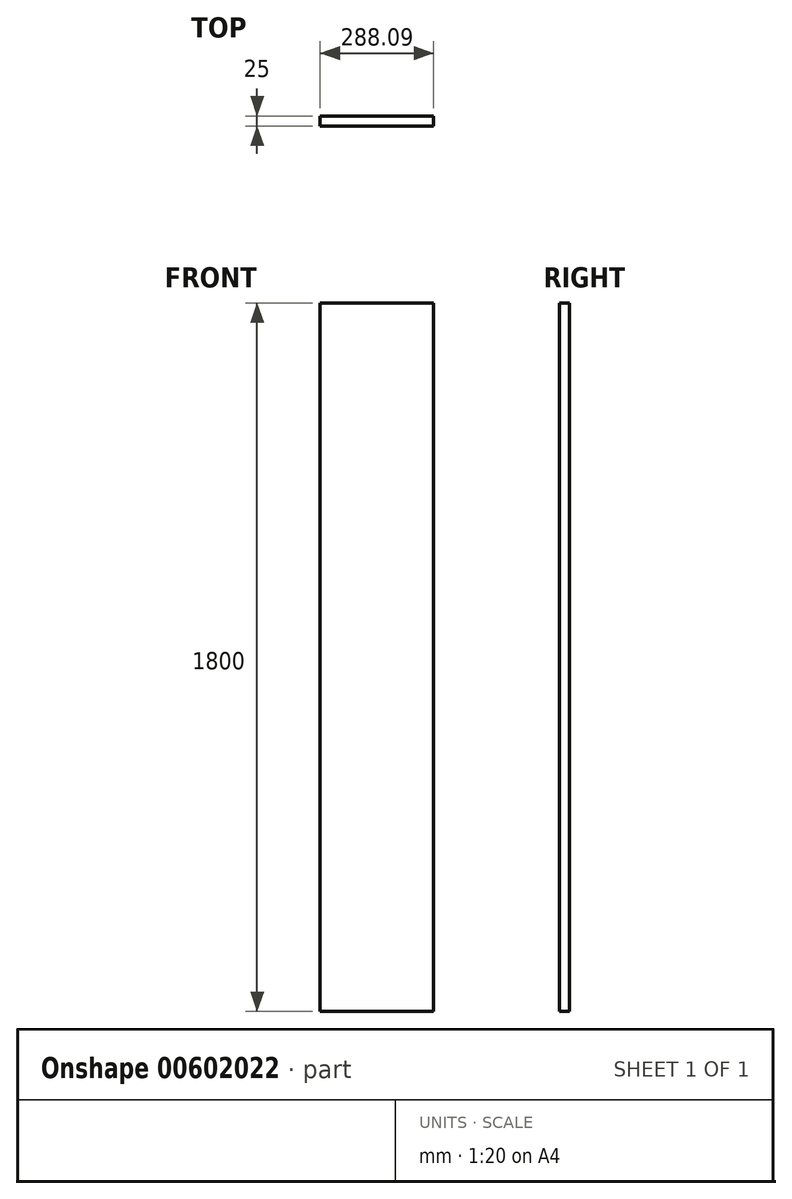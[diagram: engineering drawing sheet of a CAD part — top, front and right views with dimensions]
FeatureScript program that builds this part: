
annotation { "Feature Type Name" : "Feature", "Feature Type Description" : "" }
export const myFeature = defineFeature(function(context is Context, id is Id, definition is map)
    precondition{}
    {
        {
            var Q0;
            Q0=qCreatedBy(makeId("Front.planeOp"),FACE);
            var sketch = newSketch(context, id + "F0", { "sketchPlane" : qUnion([Q0])});
            skLineSegment(sketch, "E0.bottom", {"start": v(0, 0) * mm, "end": v(288.09, 0) * mm});
            skLineSegment(sketch, "E0.top", {"start": v(0, 1800) * mm, "end": v(288.09, 1800) * mm});
            skLineSegment(sketch, "E0.left", {"start": v(0, 0) * mm, "end": v(0, 1800) * mm});
            skLineSegment(sketch, "E0.right", {"start": v(288.09, 0) * mm, "end": v(288.09, 1800) * mm});
            skSolve(sketch);
        }
        {
            var Q0;
            Q0=makeQuery(id+"F0.imprint","IMPRINT",FACE,{"disambiguationData":[TD([[makeQuery(id+"F0.imprint","IMPRINT",EDGE,{"derivedFrom":sQuery(id+"F0.wireOp",EDGE,"E0.bottom")}),1.0]])]});
            extrude(context, id + "F1", {"entities" : qUnion([Q0]), "depth" : 25 * mm, "offsetDistance" : 25 * mm});
        }
    });
